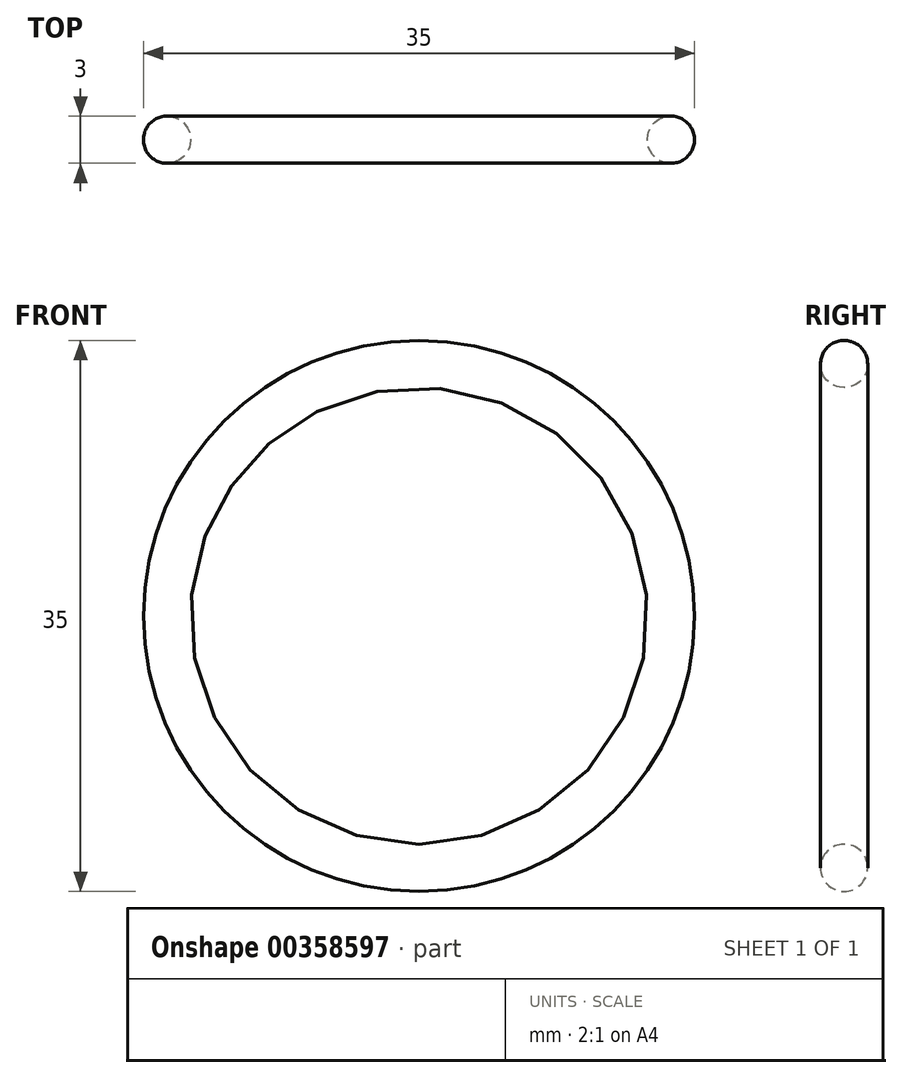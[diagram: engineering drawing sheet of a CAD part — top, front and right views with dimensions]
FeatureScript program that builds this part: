
annotation { "Feature Type Name" : "Feature", "Feature Type Description" : "" }
export const myFeature = defineFeature(function(context is Context, id is Id, definition is map)
    precondition{}
    {
        {
            var Q0;
            Q0=qCreatedBy(makeId("Top.planeOp"),FACE);
            var sketch = newSketch(context, id + "F0", { "sketchPlane" : qUnion([Q0])});
            skCircle(sketch, "E0", {"center": v(0, 0) * mm, "radius": 1.5 * mm});
            skLineSegment(sketch, "E1", {"start": v(16, -7.6) * mm, "end": v(16, 7.03) * mm});
            skSolve(sketch);
        }
        {
            var Q0;
            Q0=makeQuery(id+"F0.imprint","IMPRINT",FACE,{"disambiguationData":[TD([[makeQuery(id+"F0.imprint","IMPRINT",EDGE,{"derivedFrom":sQuery(id+"F0.wireOp",EDGE,"E0")}),1.0]])]});
            var Q1;
            Q1=sQuery(id+"F0.wireOp",EDGE,"E1");
            revolve(context, id + "F1", {"entities" : qUnion([Q0]), "axis" : qUnion([Q1]), "revolveType" : RevolveType.FULL});
        }
    });
